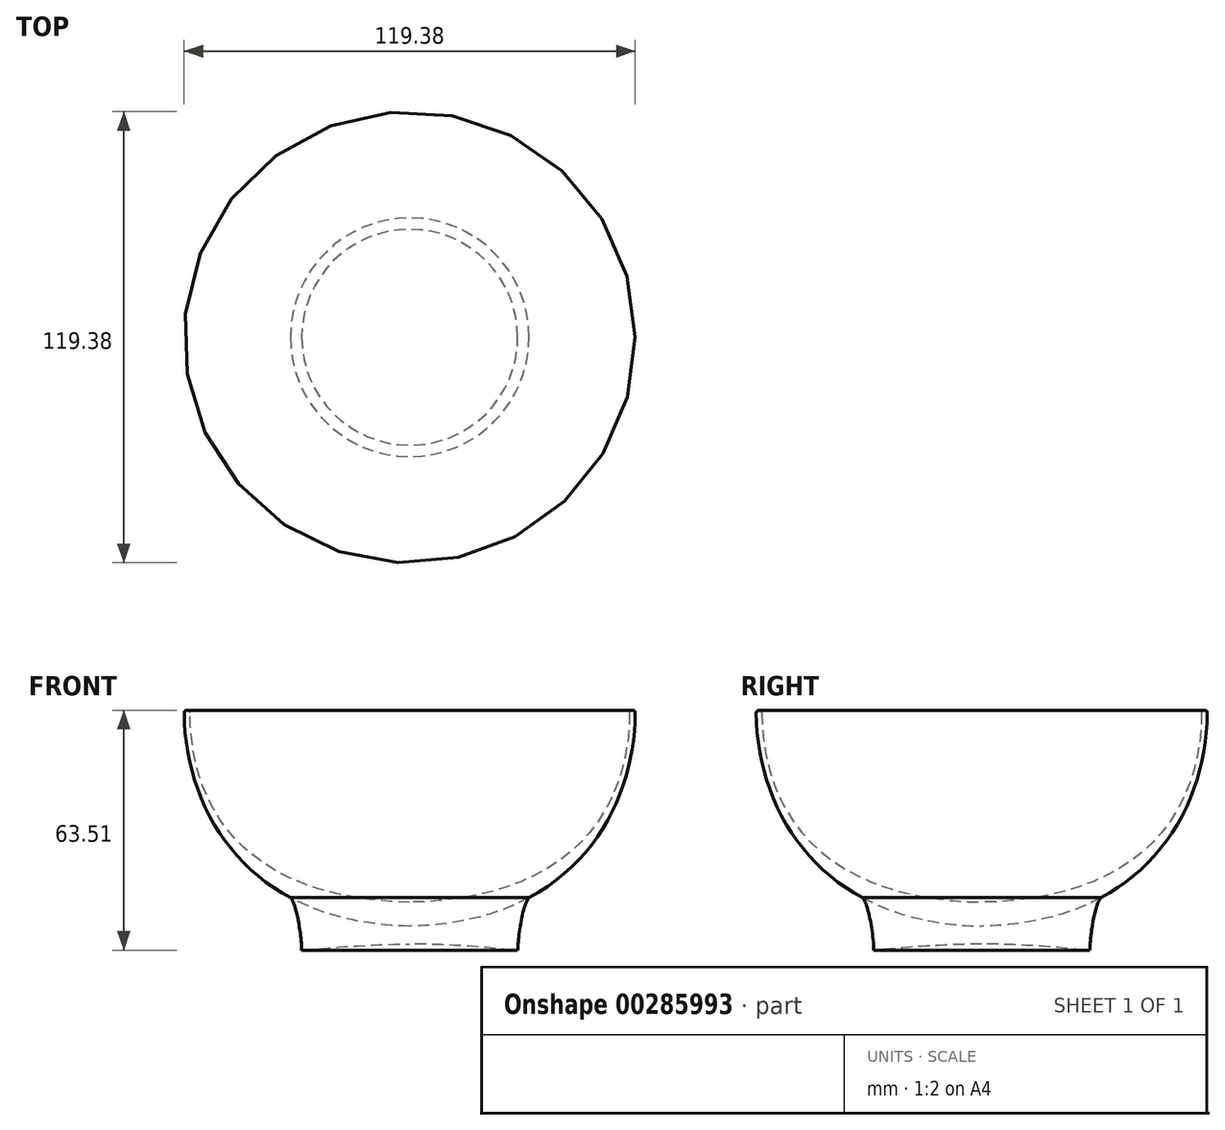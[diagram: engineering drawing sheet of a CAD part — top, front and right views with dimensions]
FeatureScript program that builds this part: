
annotation { "Feature Type Name" : "Feature", "Feature Type Description" : "" }
export const myFeature = defineFeature(function(context is Context, id is Id, definition is map)
    precondition{}
    {
        {
            var Q0;
            Q0=qCreatedBy(makeId("Front.planeOp"),FACE);
            var sketch = newSketch(context, id + "F0", { "sketchPlane" : qUnion([Q0])});
            skLineSegment(sketch, "E0", {"start": v(0, 0) * mm, "end": v(0, 148.93) * mm, "construction": true});
            skLineSegment(sketch, "E1", {"start": v(-59.69, 57.15) * mm, "end": v(59.69, 57.15) * mm});
            skFitSpline(sketch, "E2", {"points": [v(0, 0) * mm, v(-59.7, 57.15) * mm], "startDerivative": vector(-129.63, 2.3) * mm, "endDerivative": vector(0.4, 78.23) * mm});
            skFitSpline(sketch, "E3.MirrorCS", {"points": [v(0, 0) * mm, v(59.7, 57.15) * mm], "startDerivative": vector(129.63, 2.3) * mm, "endDerivative": vector(-0.4, 78.23) * mm});
            skFitSpline(sketch, "E4", {"points": [v(-28.58, -6.35) * mm, v(-31.6, 7.55) * mm], "startDerivative": vector(-0.18, 10.13) * mm, "endDerivative": vector(-5.38, 6.01) * mm});
            skFitSpline(sketch, "E5.MirrorCS", {"points": [v(28.58, -6.35) * mm, v(31.6, 7.55) * mm], "startDerivative": vector(0.18, 10.13) * mm, "endDerivative": vector(5.38, 6.01) * mm});
            skFitSpline(sketch, "E6", {"points": [v(0, 6.35) * mm, v(-58.17, 57.15) * mm], "startDerivative": vector(-129.63, 2.3) * mm, "endDerivative": vector(0.4, 78.23) * mm});
            skFitSpline(sketch, "E7.MirrorCS", {"points": [v(0, 6.35) * mm, v(58.17, 57.15) * mm], "startDerivative": vector(129.63, 2.3) * mm, "endDerivative": vector(-0.4, 78.23) * mm});
            skLineSegment(sketch, "E8", {"start": v(0, 148.93) * mm, "end": v(0, -107.9) * mm});
            skFitSpline(sketch, "E9", {"points": [v(-28.58, -6.35) * mm, v(-27.3, -6.35) * mm, v(0, -4.76) * mm, v(26.99, -6.35) * mm, v(28.58, -6.35) * mm], "startDerivative": vector(43.27, 0) * mm, "endDerivative": vector(38.64, 0) * mm});
            skSolve(sketch);
        }
        {
            var Q0;
            {var subQ4=sQuery(id+"F0.wireOp",EDGE,"E6");Q0=makeQuery(id+"F0.imprint","IMPRINT",FACE,{"disambiguationData":[TD([[makeQuery(id+"F0.imprint","IMPRINT",EDGE,{"derivedFrom":subQ4}),1.0]])]});}
            var Q1;
            Q1=sQuery(id+"F0.wireOp",EDGE,"E8");
            revolve(context, id + "F1", {"entities" : qUnion([Q0]), "axis" : qUnion([Q1]), "revolveType" : RevolveType.FULL});
        }
        {
            var Q0;
            Q0=makeQuery(id+"F1.opRevolve","SWEPT_EDGE",EDGE,{"disambiguationData":[OSD([sQuery(id+"F0.wireOp",EDGE,"E1"),sQuery(id+"F0.wireOp",EDGE,"E6")])]});
            var Q1;
            Q1=makeQuery(id+"F1.opRevolve","SWEPT_EDGE",EDGE,{"disambiguationData":[OSD([sQuery(id+"F0.wireOp",EDGE,"E1"),sQuery(id+"F0.wireOp",EDGE,"E2")])]});
            fillet(context, id + "F2", {"entities" : qUnion([Q0, Q1]), "radius" : 0.74 * mm, "tangentPropagation" : true, "allowEdgeOverflow" : false});
        }
        {
            var Q0;
            {var subQ3=sQuery(id+"F0.wireOp",EDGE,"E4");Q0=makeQuery(id+"F0.imprint","IMPRINT",FACE,{"disambiguationData":[TD([[makeQuery(id+"F0.imprint","IMPRINT",EDGE,{"derivedFrom":subQ3}),-1.0]])]});}
            var Q1;
            Q1=sQuery(id+"F0.wireOp",EDGE,"E8");
            revolve(context, id + "F3", {"entities" : qUnion([Q0]), "axis" : qUnion([Q1]), "revolveType" : RevolveType.FULL});
        }
    });
